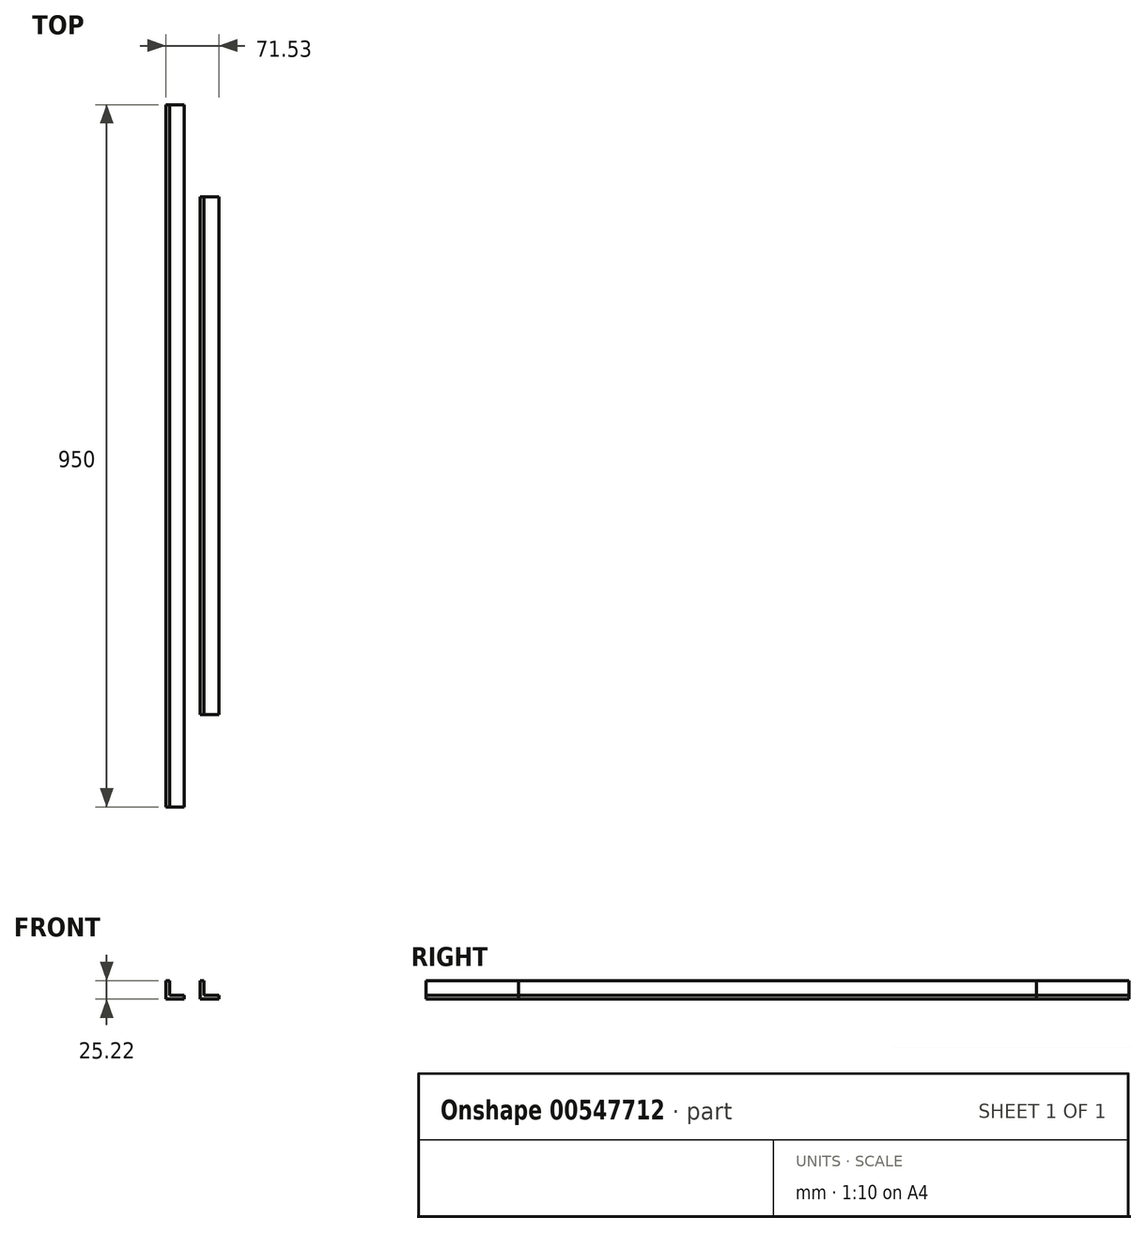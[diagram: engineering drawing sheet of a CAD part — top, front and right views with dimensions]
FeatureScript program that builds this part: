
annotation { "Feature Type Name" : "Feature", "Feature Type Description" : "" }
export const myFeature = defineFeature(function(context is Context, id is Id, definition is map)
    precondition{}
    {
        {
            var Q0;
            Q0=qCreatedBy(makeId("Front.planeOp"),FACE);
            var sketch = newSketch(context, id + "F0", { "sketchPlane" : qUnion([Q0])});
            skLineSegment(sketch, "E0", {"start": v(0, 0) * mm, "end": v(0, 25) * mm});
            skLineSegment(sketch, "E1", {"start": v(0, 25) * mm, "end": v(5, 25) * mm});
            skLineSegment(sketch, "E2", {"start": v(5, 25) * mm, "end": v(5, 5) * mm});
            skLineSegment(sketch, "E3", {"start": v(5, 5) * mm, "end": v(25, 5) * mm});
            skLineSegment(sketch, "E4", {"start": v(25, 5) * mm, "end": v(25, 0) * mm});
            skLineSegment(sketch, "E5", {"start": v(25, 0) * mm, "end": v(0, 0) * mm});
            skSolve(sketch);
        }
        {
            var Q0;
            Q0 = qSketchRegion(id + "F0", true);
            extrude(context, id + "F1", {"entities" : qUnion([Q0]), "endBound" : BoundingType.SYMMETRIC, "depth" : 950 * mm, "offsetDistance" : 25 * mm});
        }
        {
            var Q0;
            Q0=qCreatedBy(makeId("Front.planeOp"),FACE);
            var sketch = newSketch(context, id + "F2", { "sketchPlane" : qUnion([Q0])});
            skLineSegment(sketch, "E6", {"start": v(46.53, 0.22) * mm, "end": v(46.53, 25.22) * mm});
            skLineSegment(sketch, "E7", {"start": v(46.53, 25.22) * mm, "end": v(51.53, 25.22) * mm});
            skLineSegment(sketch, "E8", {"start": v(51.53, 25.22) * mm, "end": v(51.53, 5.22) * mm});
            skLineSegment(sketch, "E9", {"start": v(51.53, 5.22) * mm, "end": v(71.53, 5.22) * mm});
            skLineSegment(sketch, "E10", {"start": v(71.53, 5.22) * mm, "end": v(71.53, 0.22) * mm});
            skLineSegment(sketch, "E11", {"start": v(71.53, 0.22) * mm, "end": v(46.53, 0.22) * mm});
            skSolve(sketch);
        }
        {
            var Q0;
            Q0 = qSketchRegion(id + "F2", true);
            extrude(context, id + "F3", {"entities" : qUnion([Q0]), "endBound" : BoundingType.SYMMETRIC, "depth" : 700 * mm, "offsetDistance" : 25 * mm});
        }
    });
